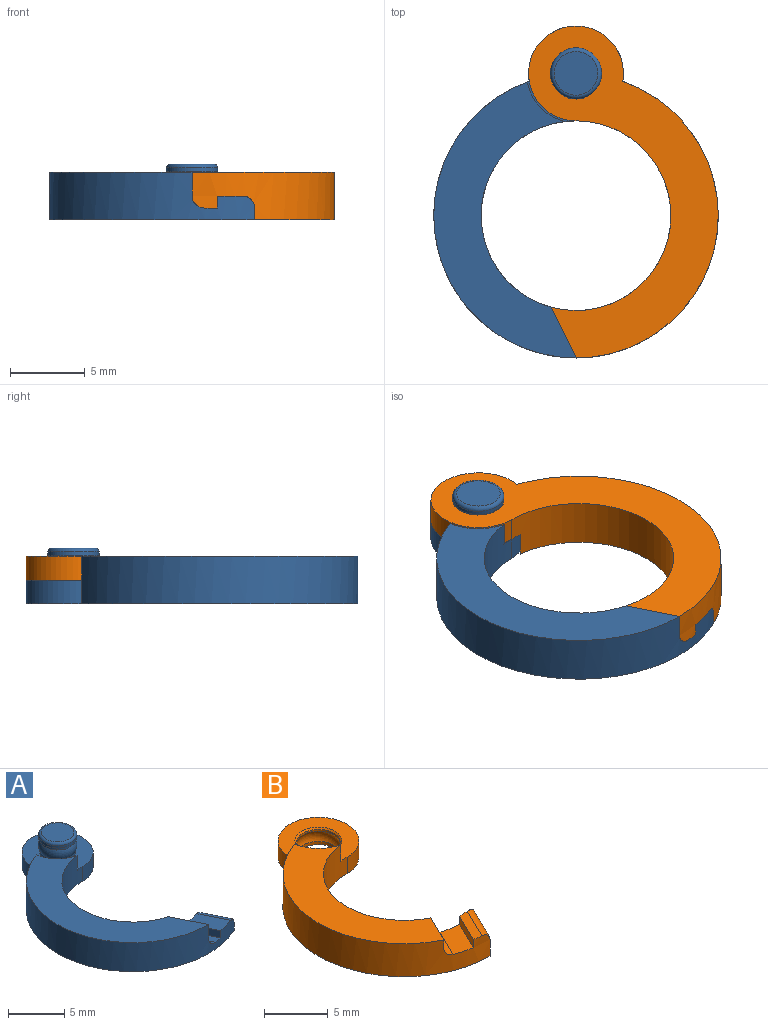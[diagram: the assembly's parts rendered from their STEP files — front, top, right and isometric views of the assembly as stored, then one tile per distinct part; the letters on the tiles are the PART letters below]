
ASSEMBLY  parts=2 mates=1
PART A: 21 faces, bbox 13.7x22.5x3.7 mm
  f0: cylinder r=1.59mm len=3.18mm, axis (0,0,-1), area 2.5mm2, adj f9,f15
  f1: plane 3.36x3.24mm, normal (0,0,1), area 5.9mm2, adj f2,f4,f11,f14
  f2: cylinder r=6.35mm len=12.7mm, axis (0,0,-1), area 62.6mm2, adj f1,f3,f5,f6,f7,f8,f9,f10
  f3: cylinder r=3.3mm len=2.65mm, axis (0,0,-1), area 6.1mm2, adj f2,f4,f6,f9
  f4: cylinder r=9.53mm len=18.52mm, axis (0,0,-1), area 90.2mm2, adj f1,f3,f5,f6,f7,f8,f9,f10
  f5: plane 3.4x1.66mm, normal (0.9,0.44,0), area 6mm2, adj f2,f4,f6,f13
  f6: plane 18.48x9.53mm, normal (0,0,1), area 68.7mm2, adj f2,f3,f4,f5
  f7: plane 22.23x13.7mm, normal (0,0,-1), area 114.9mm2, adj f2,f4,f8,f10
  f8: cylinder r=3.17mm len=6.35mm, axis (0,0,-1), area 24.6mm2, adj f2,f4,f7,f9
  f9: plane 6.43x6.39mm, normal (0,0,1), area 24.3mm2, adj f0,f2,f3,f4,f8
  f10: plane 2.85x1.39mm, normal (0.9,0.44,0), area 2.5mm2, adj f2,f4,f7,f14
  f11: plane 3.03x1.48mm, normal (-0.9,-0.44,0), area 2.7mm2, adj f1,f2,f4,f12
  f12: plane 3.17x2.38mm, normal (0,0,1), area 2.7mm2, adj f2,f4,f11,f13
  f13: cylinder r=0.79mm len=4.05mm, axis (-0.44,0.9,0), area 4.6mm2, adj f2,f4,f5,f12
  f14: cylinder r=0.79mm len=3.25mm, axis (0.44,-0.9,0), area 4mm2, adj f1,f2,f4,f10
  f15: torus R=0.5mm, axis (0,0,-1), area 11.8mm2, adj f0,f16
  f16: cylinder r=1.59mm len=3.18mm, axis (0,0,-1), area 3mm2, adj f15,f19
  f17: cylinder r=1.71mm len=3.43mm, axis (0,0,-1), area 2.7mm2, adj f19,f20
  f18: plane 2.92x2.92mm, normal (0,0,1), area 6.7mm2, adj f20
  f19: plane 3.43x3.43mm, normal (0,0,-1), area 1.3mm2, adj f16,f17
  f20: torus R=1.46mm, axis (0,0,1), area 4.1mm2, adj f17,f18
PART B: 18 faces, bbox 12.7x22.5x3.2 mm
  f0: cylinder r=1.71mm len=3.43mm, axis (0,0,-1), area 3.3mm2, adj f7,f17
  f1: plane 3.36x3.24mm, normal (0,0,1), area 5.9mm2, adj f3,f5,f12,f15
  f2: cylinder r=3.3mm len=2.65mm, axis (0,0,-1), area 6.1mm2, adj f3,f5,f6,f11
  f3: cylinder r=9.53mm len=18.52mm, axis (0,0,-1), area 79.1mm2, adj f1,f2,f4,f6,f7,f8,f9,f11
  f4: plane 2.85x1.39mm, normal (0.9,-0.44,0), area 2.5mm2, adj f3,f5,f6,f15
  f5: cylinder r=6.35mm len=12.7mm, axis (0,0,-1), area 61.7mm2, adj f1,f2,f4,f6,f7,f8,f9,f11
  f6: plane 17.51x8.79mm, normal (0,0,1), area 59.9mm2, adj f2,f3,f4,f5
  f7: plane 22.23x12.7mm, normal (0,0,-1), area 96.8mm2, adj f0,f3,f5,f8,f9
  f8: plane 3.4x1.66mm, normal (0.9,-0.44,0), area 6mm2, adj f3,f5,f7,f14
  f9: cylinder r=3.17mm len=6.35mm, axis (0,0,-1), area 24.6mm2, adj f3,f5,f7,f11
  f10: cylinder r=1.71mm len=3.43mm, axis (0,0,-1), area 1.9mm2, adj f16,f17
  f11: plane 6.43x6.39mm, normal (0,0,1), area 21.5mm2, adj f2,f3,f5,f9,f16
  f12: plane 3.03x1.48mm, normal (-0.9,0.44,0), area 2.7mm2, adj f1,f3,f5,f13
  f13: plane 3.17x2.38mm, normal (0,0,1), area 2.7mm2, adj f3,f5,f12,f14
  f14: cylinder r=0.79mm len=4.05mm, axis (-0.44,-0.9,0), area 4.6mm2, adj f3,f5,f8,f13
  f15: cylinder r=0.79mm len=3.25mm, axis (0.44,0.9,0), area 4mm2, adj f1,f3,f4,f5
  f16: cone r=1.71mm half-angle=45deg, axis (0,0,1), area 2mm2, adj f10,f11
  f17: torus R=0.84mm, axis (0,0,1), area 11.5mm2, adj f0,f10
PLACE A rot(axis=(-0.24,0.94,0.25),0deg) t=(15.88,-3.57,-4.09)mm fixed
PLACE B rot(axis=(0,-1,0),180deg) t=(15.88,-3.57,-0.92)mm
MATE revolute B.f0 <-> A.f0  axis (0,0,-1) through (15.88,5.95,-2.51)mm
